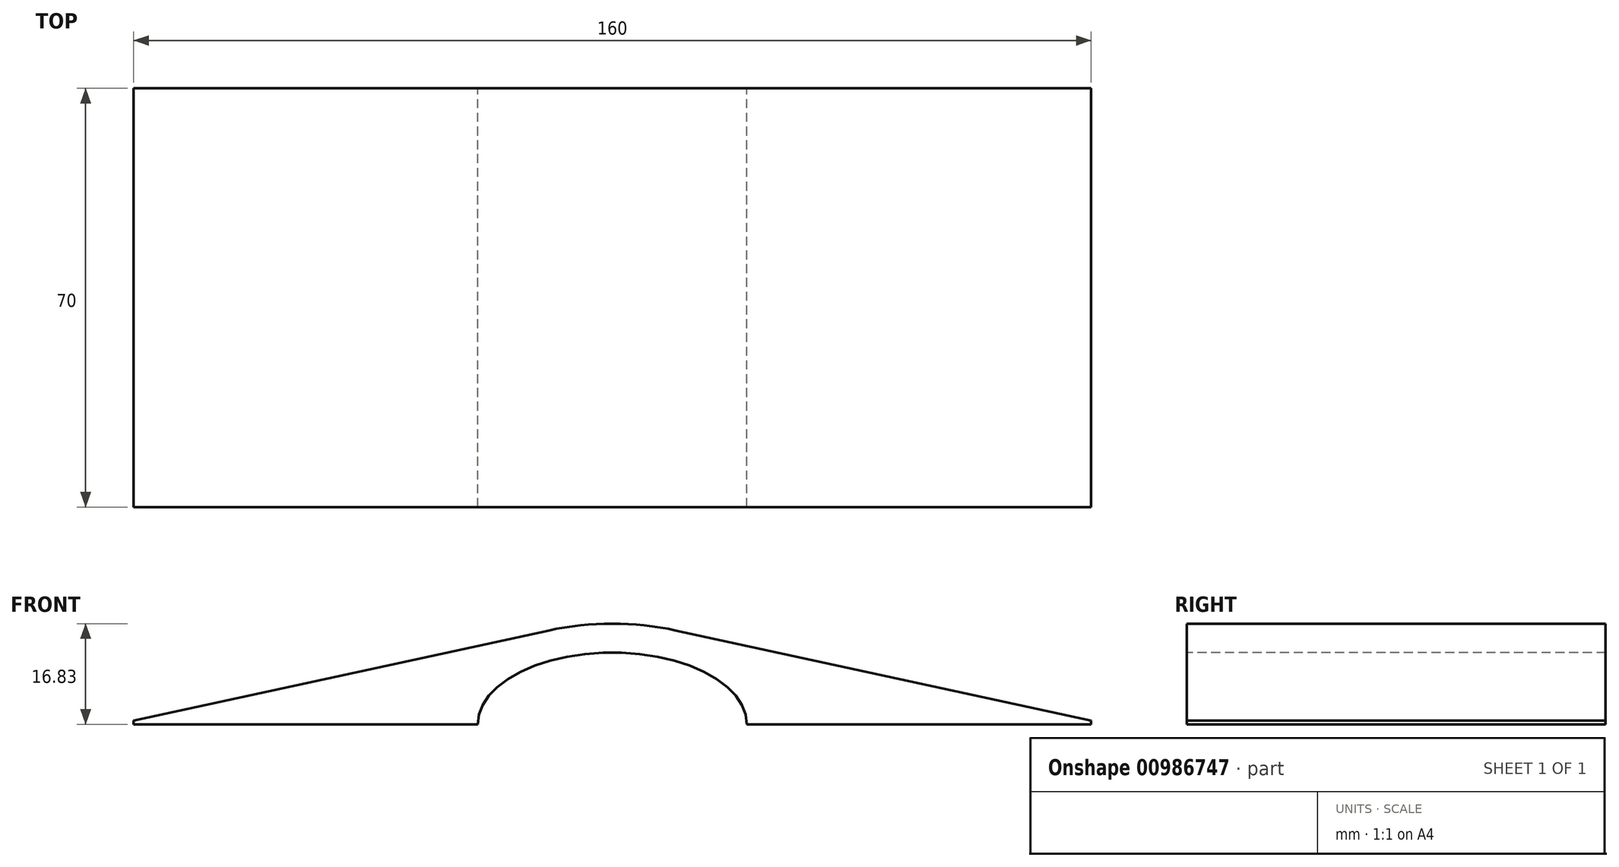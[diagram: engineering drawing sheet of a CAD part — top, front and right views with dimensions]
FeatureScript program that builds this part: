
annotation { "Feature Type Name" : "Feature", "Feature Type Description" : "" }
export const myFeature = defineFeature(function(context is Context, id is Id, definition is map)
    precondition{}
    {
        {
            var Q0;
            Q0=qCreatedBy(makeId("Front.planeOp"),FACE);
            var sketch = newSketch(context, id + "F0", { "sketchPlane" : qUnion([Q0])});
            skLineSegment(sketch, "E0", {"start": v(-80, 0) * mm, "end": v(80, 0) * mm});
            skLineSegment(sketch, "E1", {"start": v(80, 0) * mm, "end": v(80, 0.6) * mm});
            skLineSegment(sketch, "E2", {"start": v(80, 0.6) * mm, "end": v(0, 18) * mm});
            skLineSegment(sketch, "E3", {"start": v(0, 18) * mm, "end": v(-80, 0.6) * mm});
            skLineSegment(sketch, "E4", {"start": v(-80, 0.6) * mm, "end": v(-80, 0) * mm});
            skPoint(sketch, "E5.middle", {"position": v(0, 0) * mm});
            skEllipse(sketch, "E6", {"center": v(0, 0) * mm, "majorRadius": 12 * mm, "minorRadius": 22.5 * mm, "majorAxis": v(0, 1)});
            skSolve(sketch);
        }
        {
            var Q0;
            {var subQ0=sQuery(id+"F0.wireOp",EDGE,"E1");Q0=makeQuery(id+"F0.imprint","IMPRINT",FACE,{"disambiguationData":[TD([[makeQuery(id+"F0.imprint","IMPRINT",EDGE,{"derivedFrom":subQ0}),1.0]])]});}
            extrude(context, id + "F1", {"entities" : qUnion([Q0]), "depth" : 70 * mm, "offsetDistance" : 25 * mm});
        }
        {
            var Q0;
            Q0=makeQuery(id+"F1.opExtrude","SWEPT_EDGE",EDGE,{"disambiguationData":[OSD([sQuery(id+"F0.wireOp",EDGE,"E2"),sQuery(id+"F0.wireOp",EDGE,"E3")])]});
            fillet(context, id + "F2", {"entities" : qUnion([Q0]), "radius" : 50 * mm, "tangentPropagation" : true, "allowEdgeOverflow" : false});
        }
    });
